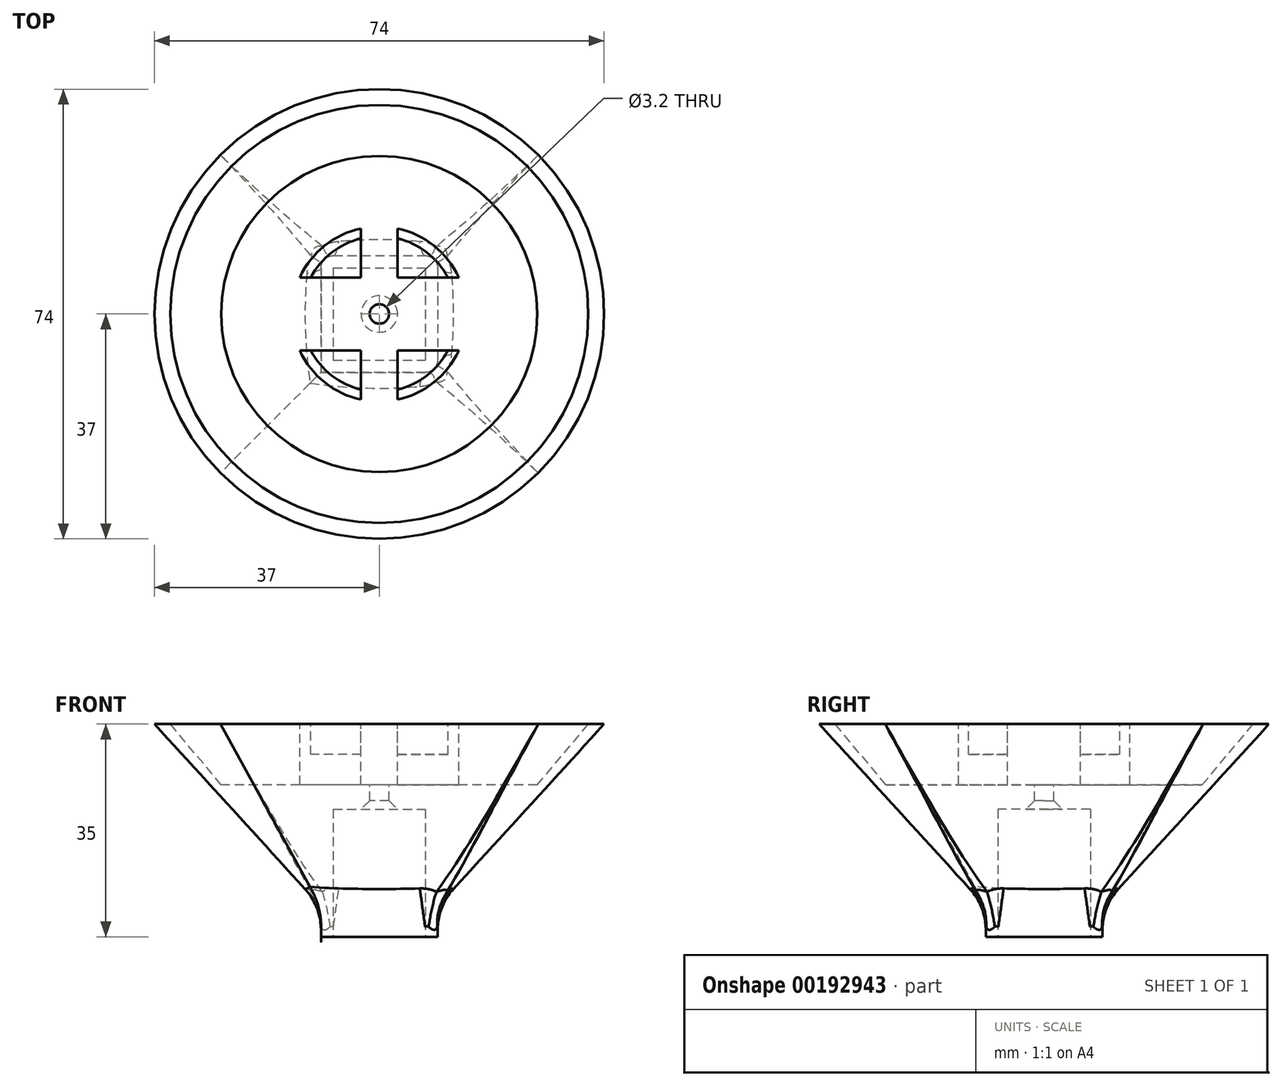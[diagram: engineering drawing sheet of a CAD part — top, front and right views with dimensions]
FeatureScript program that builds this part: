
annotation { "Feature Type Name" : "Feature", "Feature Type Description" : "" }
export const myFeature = defineFeature(function(context is Context, id is Id, definition is map)
    precondition{}
    {
        {
            var Q0;
            Q0=qCreatedBy(makeId("Top.planeOp"),FACE);
            var sketch = newSketch(context, id + "F0", { "sketchPlane" : qUnion([Q0])});
            skCircle(sketch, "E0", {"center": v(0, 0) * mm, "radius": 37 * mm});
            skSolve(sketch);
        }
        {
            var Q0;
            Q0=qCreatedBy(makeId("Top.planeOp"),FACE);
            cPlane(context, id + "F1", {"entities" : qUnion([Q0]), "cplaneType" : CPlaneType.OFFSET, "offset" : 30 * mm, "oppositeDirection" : true, "width" : 150 * mm, "height" : 150 * mm});
        }
        {
            var Q0;
            Q0=qCreatedBy(id+"F1.planeOp",FACE);
            var sketch = newSketch(context, id + "F2", { "sketchPlane" : qUnion([Q0])});
            skLineSegment(sketch, "E1.bottom", {"start": v(-9.6, 9.6) * mm, "end": v(9.6, 9.6) * mm});
            skLineSegment(sketch, "E1.top", {"start": v(-9.6, -9.6) * mm, "end": v(9.6, -9.6) * mm});
            skLineSegment(sketch, "E1.left", {"start": v(-9.6, 9.6) * mm, "end": v(-9.6, -9.6) * mm});
            skLineSegment(sketch, "E1.right", {"start": v(9.6, 9.6) * mm, "end": v(9.6, -9.6) * mm});
            skPoint(sketch, "E1.middle", {"position": v(0, 0) * mm});
            skSolve(sketch);
        }
        {
            var Q0;
            Q0=makeQuery(id+"F2.imprint","IMPRINT",FACE,{"disambiguationData":[TD([[makeQuery(id+"F2.imprint","IMPRINT",EDGE,{"derivedFrom":sQuery(id+"F2.wireOp",EDGE,"E1.bottom")}),-1.0]])]});
            var Q1;
            Q1=makeQuery(id+"F0.imprint","IMPRINT",FACE,{"disambiguationData":[TD([[makeQuery(id+"F0.imprint","IMPRINT",EDGE,{"derivedFrom":sQuery(id+"F0.wireOp",EDGE,"E0")}),1.0]])]});
            loft(context, id + "F3", {"sheetProfilesArray" : [{ "sheetProfileEntities" : qUnion([Q0]) }, { "sheetProfileEntities" : qUnion([Q1]) }]});
        }
        {
            var Q0;
            Q0=makeQuery(id+"F3.opLoft","CAP_FACE",FACE,{"disambiguationData":[OSD([makeQuery(id+"F2.imprint","IMPRINT",FACE,{"disambiguationData":[TD([[makeQuery(id+"F2.imprint","IMPRINT",EDGE,{"derivedFrom":sQuery(id+"F2.wireOp",EDGE,"E1.bottom")}),-1.0]])]})])],"isStart":true});
            var sketch = newSketch(context, id + "F4", { "sketchPlane" : qUnion([Q0])});
            skLineSegment(sketch, "E2.bottom", {"start": v(-7.6, -7.6) * mm, "end": v(7.6, -7.6) * mm});
            skLineSegment(sketch, "E2.top", {"start": v(-7.6, 7.6) * mm, "end": v(7.6, 7.6) * mm});
            skLineSegment(sketch, "E2.left", {"start": v(-7.6, -7.6) * mm, "end": v(-7.6, 7.6) * mm});
            skLineSegment(sketch, "E2.right", {"start": v(7.6, -7.6) * mm, "end": v(7.6, 7.6) * mm});
            skPoint(sketch, "E2.middle", {"position": v(0, 0) * mm});
            skSolve(sketch);
        }
        {
            var Q0;
            Q0 = qSketchRegion(id + "F4", true);
            extrude(context, id + "F5", {"entities" : qUnion([Q0]), "operationType" : NewBodyOperationType.REMOVE, "oppositeDirection" : true, "depth" : 16 * mm});
        }
        {
            var Q0;
            Q0=makeQuery(id+"F3.opLoft","CAP_FACE",FACE,{"disambiguationData":[OSD([makeQuery(id+"F0.imprint","IMPRINT",FACE,{"disambiguationData":[TD([[makeQuery(id+"F0.imprint","IMPRINT",EDGE,{"derivedFrom":sQuery(id+"F0.wireOp",EDGE,"E0")}),1.0]])]})])],"isStart":true});
            var sketch = newSketch(context, id + "F6", { "sketchPlane" : qUnion([Q0])});
            skCircle(sketch, "E3", {"center": v(0, 0) * mm, "radius": 12.8 * mm});
            skSolve(sketch);
        }
        {
            var Q0;
            Q0 = qSketchRegion(id + "F6", true);
            extrude(context, id + "F7", {"entities" : qUnion([Q0]), "operationType" : NewBodyOperationType.REMOVE, "oppositeDirection" : true, "depth" : 5 * mm});
        }
        {
            var Q0;
            Q0=makeQuery(id+"F3.opLoft","CAP_FACE",FACE,{"disambiguationData":[OSD([makeQuery(id+"F0.imprint","IMPRINT",FACE,{"disambiguationData":[TD([[makeQuery(id+"F0.imprint","IMPRINT",EDGE,{"derivedFrom":sQuery(id+"F0.wireOp",EDGE,"E0")}),1.0]])]})])],"isStart":true});
            var sketch = newSketch(context, id + "F8", { "sketchPlane" : qUnion([Q0])});
            skCircle(sketch, "E4.0", {"center": v(0, 0) * mm, "radius": 14.4 * mm});
            skCircle(sketch, "E5", {"center": v(0, 0) * mm, "radius": 34.4 * mm});
            skSolve(sketch);
        }
        {
            var Q0;
            Q0 = qSketchRegion(id + "F8", true);
            extrude(context, id + "F9", {"entities" : qUnion([Q0]), "operationType" : NewBodyOperationType.REMOVE, "oppositeDirection" : true, "depth" : 10 * mm, "hasDraft" : true, "draftAngle" : 40 * degree, "draftPullDirection" : true});
        }
        {
            var Q0;
            Q0=makeQuery(id+"F9.boolean.opBoolean","SPLIT",FACE,{"disambiguationData":[TD([makeQuery(id+"F7.boolean.opBoolean","COPY",FACE,{"derivedFrom":makeQuery(id+"F7.opExtrude","SWEPT_FACE",FACE,{"disambiguationData":[OSD([sQuery(id+"F6.wireOp",EDGE,"E3")])]})})])],"derivedFrom":makeQuery(id+"F3.opLoft","CAP_FACE",FACE,{"disambiguationData":[OSD([makeQuery(id+"F0.imprint","IMPRINT",FACE,{"disambiguationData":[TD([[makeQuery(id+"F0.imprint","IMPRINT",EDGE,{"derivedFrom":sQuery(id+"F0.wireOp",EDGE,"E0")}),1.0]])]})])],"isStart":true})});
            var sketch = newSketch(context, id + "F10", { "sketchPlane" : qUnion([Q0])});
            skCircle(sketch, "E6.0", {"center": v(0, 0) * mm, "radius": 14.4 * mm});
            skCircle(sketch, "E7.0", {"center": v(0, 0) * mm, "radius": 22.8 * mm});
            skSolve(sketch);
        }
        {
            var Q0;
            Q0 = qSketchRegion(id + "F10", true);
            var Q1;
            Q1=makeQuery(id+"F9.boolean.opBoolean","COPY",FACE,{"derivedFrom":makeQuery(id+"F9.opExtrude","CAP_FACE",FACE,{"disambiguationData":[OSD([sQuery(id+"F8.wireOp",EDGE,"E4.0"),sQuery(id+"F8.wireOp",EDGE,"E5")])],"isStart":false})});
            extrude(context, id + "F11", {"entities" : qUnion([Q0]), "operationType" : NewBodyOperationType.REMOVE, "endBound" : BoundingType.UP_TO_SURFACE, "oppositeDirection" : true, "endBoundEntityFace" : qUnion([Q1]), "depth" : 25 * mm});
        }
        {
            var Q0;
            Q0=makeQuery(id+"F9.boolean.opBoolean","SPLIT",FACE,{"disambiguationData":[TD([makeQuery(id+"F7.boolean.opBoolean","COPY",FACE,{"derivedFrom":makeQuery(id+"F7.opExtrude","SWEPT_FACE",FACE,{"disambiguationData":[OSD([sQuery(id+"F6.wireOp",EDGE,"E3")])]})})])],"derivedFrom":makeQuery(id+"F3.opLoft","CAP_FACE",FACE,{"disambiguationData":[OSD([makeQuery(id+"F0.imprint","IMPRINT",FACE,{"disambiguationData":[TD([[makeQuery(id+"F0.imprint","IMPRINT",EDGE,{"derivedFrom":sQuery(id+"F0.wireOp",EDGE,"E0")}),1.0]])]})])],"isStart":true})});
            var sketch = newSketch(context, id + "F12", { "sketchPlane" : qUnion([Q0])});
            skLineSegment(sketch, "E8.bottom", {"start": v(-3, -20) * mm, "end": v(3, -20) * mm});
            skLineSegment(sketch, "E8.top", {"start": v(-3, 20) * mm, "end": v(3, 20) * mm});
            skLineSegment(sketch, "E8.left", {"start": v(-3, -20) * mm, "end": v(-3, 20) * mm});
            skLineSegment(sketch, "E8.right", {"start": v(3, -20) * mm, "end": v(3, 20) * mm});
            skPoint(sketch, "E8.middle", {"position": v(0, 0) * mm});
            skLineSegment(sketch, "E9.bottom", {"start": v(19.99, 6) * mm, "end": v(-19.99, 6) * mm});
            skLineSegment(sketch, "E9.top", {"start": v(19.99, -6) * mm, "end": v(-19.99, -6) * mm});
            skLineSegment(sketch, "E9.left", {"start": v(19.99, 6) * mm, "end": v(19.99, -6) * mm});
            skLineSegment(sketch, "E9.right", {"start": v(-19.99, 6) * mm, "end": v(-19.99, -6) * mm});
            skSolve(sketch);
        }
        {
            var Q0;
            Q0 = qSketchRegion(id + "F12", true);
            extrude(context, id + "F13", {"entities" : qUnion([Q0]), "operationType" : NewBodyOperationType.REMOVE, "oppositeDirection" : true, "depth" : 10 * mm});
        }
        {
            var Q0;
            Q0=makeQuery(id+"F13.boolean.opBoolean","MERGE",FACE,{"derivedFrom":[makeQuery(id+"F11.boolean.opBoolean","MERGE",FACE,{"derivedFrom":[makeQuery(id+"F9.boolean.opBoolean","COPY",FACE,{"derivedFrom":makeQuery(id+"F9.opExtrude","CAP_FACE",FACE,{"disambiguationData":[OSD([sQuery(id+"F8.wireOp",EDGE,"E4.0"),sQuery(id+"F8.wireOp",EDGE,"E5")])],"isStart":false})})],"fromTools":[makeQuery(id+"F11.opExtrude","CAP_FACE",FACE,{"disambiguationData":[OSD([sQuery(id+"F10.wireOp",EDGE,"E6.0"),sQuery(id+"F10.wireOp",EDGE,"E7.0")])],"isStart":false})]})],"fromTools":[makeQuery(id+"F13.opExtrude","CAP_FACE",FACE,{"disambiguationData":[OSD([sQuery(id+"F12.wireOp",EDGE,"E8.bottom"),sQuery(id+"F12.wireOp",EDGE,"E8.top"),sQuery(id+"F12.wireOp",EDGE,"E8.left"),sQuery(id+"F12.wireOp",EDGE,"E8.right"),sQuery(id+"F12.wireOp",EDGE,"E9.bottom"),sQuery(id+"F12.wireOp",EDGE,"E9.top"),sQuery(id+"F12.wireOp",EDGE,"E9.left"),sQuery(id+"F12.wireOp",EDGE,"E9.right")])],"isStart":false})]});
            var sketch = newSketch(context, id + "F14", { "sketchPlane" : qUnion([Q0])});
            skCircle(sketch, "E10", {"center": v(0, 0) * mm, "radius": 1.6 * mm});
            skSolve(sketch);
        }
        {
            var Q0;
            Q0 = qSketchRegion(id + "F14", true);
            extrude(context, id + "F15", {"entities" : qUnion([Q0]), "operationType" : NewBodyOperationType.REMOVE, "oppositeDirection" : true, "depth" : 25 * mm});
        }
        {
            var Q0;
            Q0=makeQuery(id+"F3.opLoft","SWEPT_EDGE",EDGE,{"disambiguationData":[OSD([sQuery(id+"F0.wireOp",EDGE,"E0"),sQuery(id+"F2.wireOp",EDGE,"E1.top"),sQuery(id+"F2.wireOp",EDGE,"E1.left"),sQuery(id+"F2.wireOp",EDGE,"E1.right")])]});
            var Q1;
            Q1=makeQuery(id+"F3.opLoft","SWEPT_EDGE",EDGE,{"disambiguationData":[OSD([sQuery(id+"F0.wireOp",EDGE,"E0"),sQuery(id+"F2.wireOp",EDGE,"E1.bottom"),sQuery(id+"F2.wireOp",EDGE,"E1.top"),sQuery(id+"F2.wireOp",EDGE,"E1.right")])]});
            var Q2;
            Q2=makeQuery(id+"F3.opLoft","SWEPT_EDGE",EDGE,{"disambiguationData":[OSD([sQuery(id+"F2.wireOp",EDGE,"E1.bottom"),sQuery(id+"F2.wireOp",EDGE,"E1.left")])]});
            var Q3;
            Q3=makeQuery(id+"F3.opLoft","SWEPT_EDGE",EDGE,{"disambiguationData":[OSD([sQuery(id+"F0.wireOp",EDGE,"E0"),sQuery(id+"F2.wireOp",EDGE,"E1.bottom"),sQuery(id+"F2.wireOp",EDGE,"E1.top"),sQuery(id+"F2.wireOp",EDGE,"E1.left")])]});
            fillet(context, id + "F16", {"entities" : qUnion([Q0, Q1, Q2, Q3]), "radius" : 2.5 * mm, "tangentPropagation" : true, "allowEdgeOverflow" : false});
        }
        {
            var Q0;
            Q0=makeQuery(id+"F3.opLoft","CAP_FACE",FACE,{"disambiguationData":[OSD([makeQuery(id+"F2.imprint","IMPRINT",FACE,{"disambiguationData":[TD([[makeQuery(id+"F2.imprint","IMPRINT",EDGE,{"derivedFrom":sQuery(id+"F2.wireOp",EDGE,"E1.bottom")}),-1.0]])]})])],"isStart":true});
            extrude(context, id + "F17", {"entities" : qUnion([Q0]), "operationType" : NewBodyOperationType.ADD, "depth" : 5 * mm});
        }
        {
            var Q0;
            {var subQ0=sQuery(id+"F2.wireOp",EDGE,"E1.right");var subQ1=sQuery(id+"F2.wireOp",EDGE,"E1.left");var subQ2=sQuery(id+"F2.wireOp",EDGE,"E1.top");Q0=makeQuery(id+"F17.boolean.opBoolean","MERGE",EDGE,{"derivedFrom":[makeQuery(id+"F3.opLoft","MID_CAP_EDGE",EDGE,{"disambiguationData":[OSD([subQ2,subQ1,subQ0])],"capPos":0.0}),makeQuery(id+"F17.opExtrude","CAP_EDGE",EDGE,{"disambiguationData":[OSD([subQ2,subQ1,subQ0])],"isStart":true})]});}
            fillet(context, id + "F18", {"entities" : qUnion([Q0]), "radius" : 10 * mm, "tangentPropagation" : true, "allowEdgeOverflow" : false});
        }
        {
            var Q0;
            Q0=makeQuery(id+"F15.boolean.opBoolean","INTERSECT",EDGE,{"derivedFrom":[makeQuery(id+"F5.boolean.opBoolean","COPY",FACE,{"derivedFrom":makeQuery(id+"F5.opExtrude","CAP_FACE",FACE,{"disambiguationData":[OSD([sQuery(id+"F4.wireOp",EDGE,"E2.bottom"),sQuery(id+"F4.wireOp",EDGE,"E2.top"),sQuery(id+"F4.wireOp",EDGE,"E2.left"),sQuery(id+"F4.wireOp",EDGE,"E2.right")])],"isStart":false})}),makeQuery(id+"F15.opExtrude","SWEPT_FACE",FACE,{"disambiguationData":[OSD([sQuery(id+"F14.wireOp",EDGE,"E10")])]})]});
            chamfer(context, id + "F19", {"entities" : qUnion([Q0]), "width" : 1.4 * mm, "tangentPropagation" : true});
        }
    });
